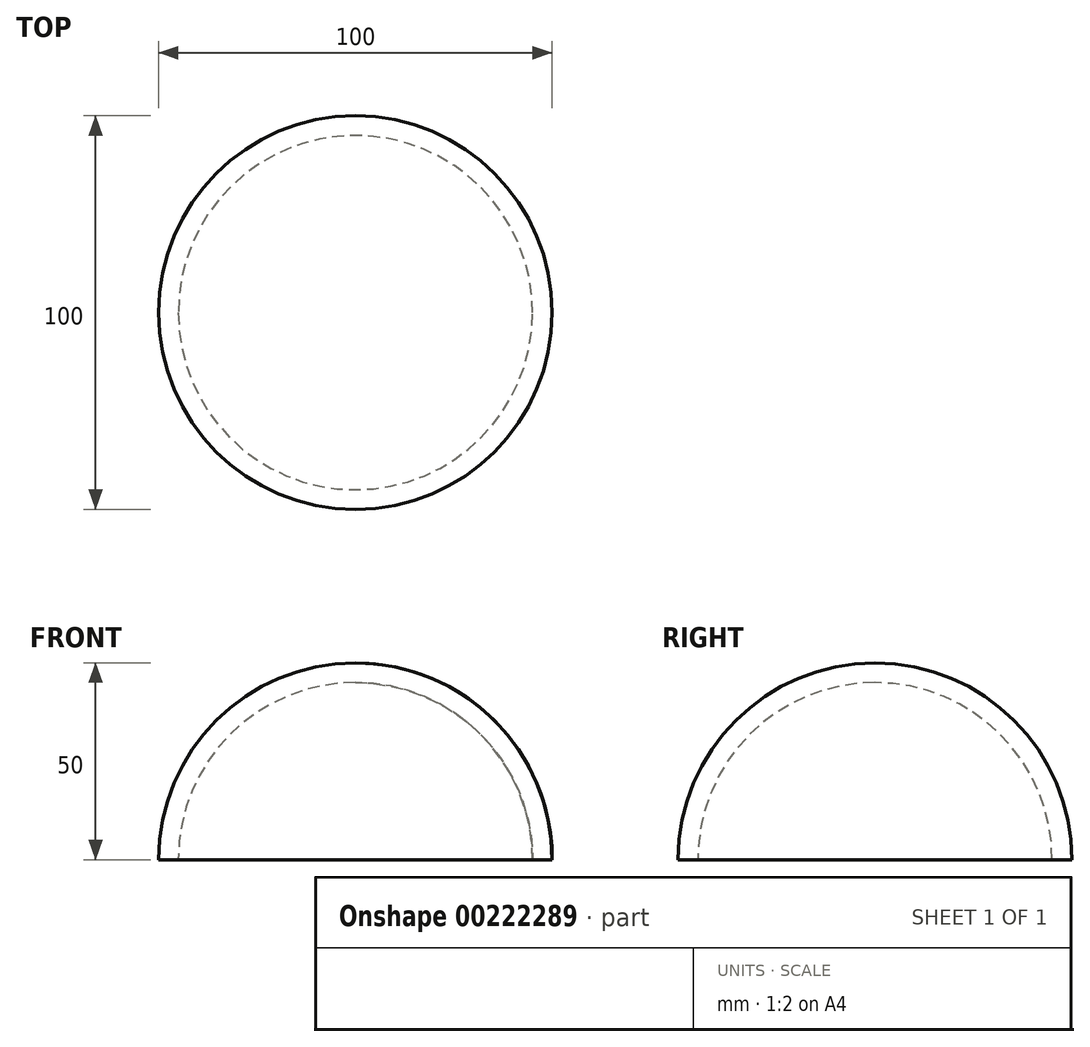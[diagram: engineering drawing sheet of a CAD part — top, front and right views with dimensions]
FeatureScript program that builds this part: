
annotation { "Feature Type Name" : "Feature", "Feature Type Description" : "" }
export const myFeature = defineFeature(function(context is Context, id is Id, definition is map)
    precondition{}
    {
        {
            var Q0;
            Q0=qCreatedBy(makeId("Front.planeOp"),FACE);
            var sketch = newSketch(context, id + "F0", { "sketchPlane" : qUnion([Q0])});
            skPoint(sketch, "E0", {"position": v(0, 0) * mm});
            skArc(sketch, "E1", {"start": v(50, 0) * mm, "mid": v(35.36, 35.36) * mm, "end": v(0, 50) * mm});
            skLineSegment(sketch, "E2", {"start": v(0, 0) * mm, "end": v(0, 50) * mm});
            skLineSegment(sketch, "E3", {"start": v(50, 0) * mm, "end": v(45, 0) * mm});
            skArc(sketch, "E4", {"start": v(45, 0) * mm, "mid": v(31.82, 31.82) * mm, "end": v(0, 45) * mm});
            skSolve(sketch);
        }
        {
            var Q0;
            {var subQ0=sQuery(id+"F0.wireOp",EDGE,"E1");Q0=makeQuery(id+"F0.imprint","IMPRINT",FACE,{"disambiguationData":[TD([[makeQuery(id+"F0.imprint","IMPRINT",EDGE,{"derivedFrom":subQ0}),1.0]])]});}
            var Q1;
            Q1=sQuery(id+"F0.wireOp",EDGE,"E2");
            revolve(context, id + "F1", {"entities" : qUnion([Q0]), "axis" : qUnion([Q1]), "revolveType" : RevolveType.FULL});
        }
    });
